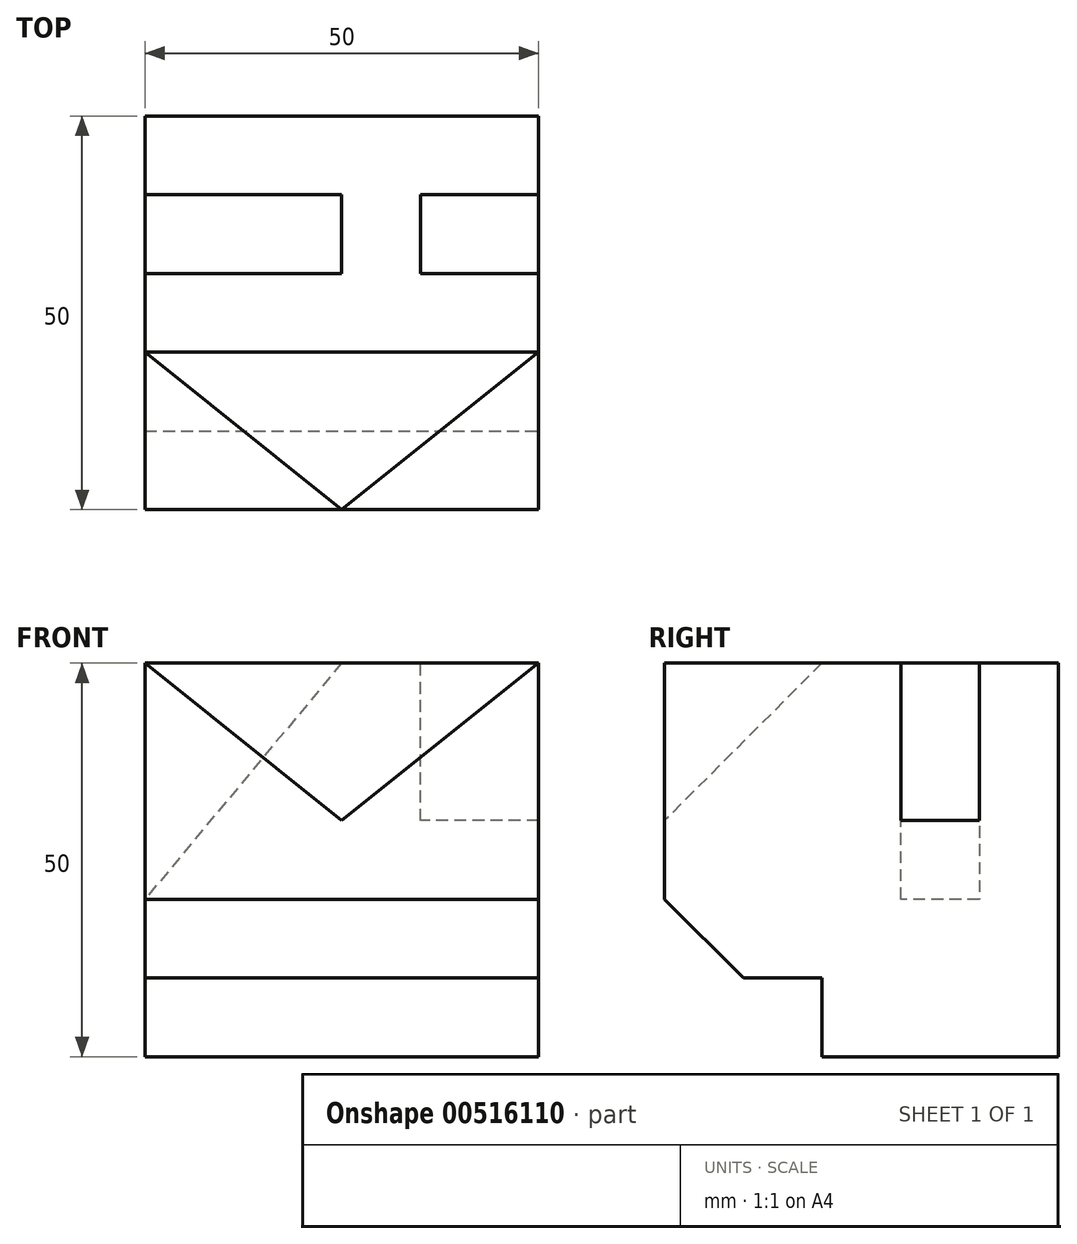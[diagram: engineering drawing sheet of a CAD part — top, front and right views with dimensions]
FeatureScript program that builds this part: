
annotation { "Feature Type Name" : "Feature", "Feature Type Description" : "" }
export const myFeature = defineFeature(function(context is Context, id is Id, definition is map)
    precondition{}
    {
        {
            var Q0;
            Q0=qCreatedBy(makeId("Top.planeOp"),FACE);
            var sketch = newSketch(context, id + "F0", { "sketchPlane" : qUnion([Q0])});
            skLineSegment(sketch, "E0.bottom", {"start": v(0, 0) * mm, "end": v(50, 0) * mm});
            skLineSegment(sketch, "E0.top", {"start": v(0, 50) * mm, "end": v(50, 50) * mm});
            skLineSegment(sketch, "E0.left", {"start": v(0, 0) * mm, "end": v(0, 50) * mm});
            skLineSegment(sketch, "E0.right", {"start": v(50, 0) * mm, "end": v(50, 50) * mm});
            skSolve(sketch);
        }
        {
            var Q0;
            Q0=makeQuery(id+"F0.imprint","IMPRINT",FACE,{"disambiguationData":[TD([[makeQuery(id+"F0.imprint","IMPRINT",EDGE,{"derivedFrom":sQuery(id+"F0.wireOp",EDGE,"E0.bottom")}),1.0]])]});
            extrude(context, id + "F1", {"entities" : qUnion([Q0]), "depth" : 50 * mm, "offsetDistance" : 25 * mm});
        }
        {
            var Q0;
            Q0=makeQuery(id+"F1.opExtrude","SWEPT_FACE",FACE,{"disambiguationData":[OSD([sQuery(id+"F0.wireOp",EDGE,"E0.right")])]});
            var sketch = newSketch(context, id + "F2", { "sketchPlane" : qUnion([Q0])});
            skLineSegment(sketch, "E1.bottom", {"start": v(0, 0) * mm, "end": v(20, 0) * mm});
            skLineSegment(sketch, "E1.top", {"start": v(0, 10) * mm, "end": v(20, 10) * mm});
            skLineSegment(sketch, "E1.left", {"start": v(0, 0) * mm, "end": v(0, 10) * mm});
            skLineSegment(sketch, "E1.right", {"start": v(20, 0) * mm, "end": v(20, 10) * mm});
            skSolve(sketch);
        }
        {
            var Q0;
            Q0=makeQuery(id+"F2.imprint","IMPRINT",FACE,{"disambiguationData":[TD([[makeQuery(id+"F2.imprint","IMPRINT",EDGE,{"derivedFrom":sQuery(id+"F2.wireOp",EDGE,"E1.bottom")}),1.0]])]});
            extrude(context, id + "F3", {"entities" : qUnion([Q0]), "operationType" : NewBodyOperationType.REMOVE, "endBound" : BoundingType.THROUGH_ALL, "oppositeDirection" : true, "depth" : 25 * mm, "offsetDistance" : 25 * mm});
        }
        {
            var Q0;
            Q0=makeQuery(id+"F1.opExtrude","SWEPT_FACE",FACE,{"disambiguationData":[OSD([sQuery(id+"F0.wireOp",EDGE,"E0.right")])]});
            var sketch = newSketch(context, id + "F4", { "sketchPlane" : qUnion([Q0])});
            skLineSegment(sketch, "E2", {"start": v(0, 10) * mm, "end": v(10, 10) * mm});
            skLineSegment(sketch, "E3", {"start": v(10, 10) * mm, "end": v(0, 20) * mm});
            skLineSegment(sketch, "E4", {"start": v(0, 20) * mm, "end": v(0, 10) * mm});
            skSolve(sketch);
        }
        {
            var Q0;
            Q0=makeQuery(id+"F4.imprint","IMPRINT",FACE,{"disambiguationData":[TD([[makeQuery(id+"F4.imprint","IMPRINT",EDGE,{"derivedFrom":sQuery(id+"F4.wireOp",EDGE,"E2")}),1.0]])]});
            extrude(context, id + "F5", {"entities" : qUnion([Q0]), "operationType" : NewBodyOperationType.REMOVE, "endBound" : BoundingType.THROUGH_ALL, "oppositeDirection" : true, "depth" : 25 * mm, "offsetDistance" : 25 * mm});
        }
        {
            var Q0;
            Q0=makeQuery(id+"F1.opExtrude","CAP_FACE",FACE,{"disambiguationData":[OSD([sQuery(id+"F0.wireOp",EDGE,"E0.bottom"),sQuery(id+"F0.wireOp",EDGE,"E0.top"),sQuery(id+"F0.wireOp",EDGE,"E0.left"),sQuery(id+"F0.wireOp",EDGE,"E0.right")])],"isStart":false});
            var sketch = newSketch(context, id + "F6", { "sketchPlane" : qUnion([Q0])});
            skLineSegment(sketch, "E5.bottom", {"start": v(0, 40) * mm, "end": v(25, 40) * mm});
            skLineSegment(sketch, "E5.top", {"start": v(0, 30) * mm, "end": v(25, 30) * mm});
            skLineSegment(sketch, "E5.left", {"start": v(0, 40) * mm, "end": v(0, 30) * mm});
            skLineSegment(sketch, "E5.right", {"start": v(25, 40) * mm, "end": v(25, 30) * mm});
            skSolve(sketch);
        }
        {
            var Q0;
            Q0=makeQuery(id+"F1.opExtrude","SWEPT_FACE",FACE,{"disambiguationData":[OSD([sQuery(id+"F0.wireOp",EDGE,"E0.bottom")])]});
            var sketch = newSketch(context, id + "F7", { "sketchPlane" : qUnion([Q0])});
            skLineSegment(sketch, "E6", {"start": v(25, 50) * mm, "end": v(0, 20) * mm});
            skSolve(sketch);
        }
        {
            var Q0;
            Q0=makeQuery(id+"F6.imprint","IMPRINT",FACE,{"disambiguationData":[TD([[makeQuery(id+"F6.imprint","IMPRINT",EDGE,{"derivedFrom":sQuery(id+"F6.wireOp",EDGE,"E5.bottom")}),-1.0]])]});
            var Q1;
            Q1=sQuery(id+"F7.wireOp",EDGE,"E6");
            sweep(context, id + "F8", {"operationType" : NewBodyOperationType.REMOVE, "profiles" : qUnion([Q0]), "path" : qUnion([Q1])});
        }
        {
            var Q0;
            Q0=makeQuery(id+"F1.opExtrude","CAP_FACE",FACE,{"disambiguationData":[OSD([sQuery(id+"F0.wireOp",EDGE,"E0.bottom"),sQuery(id+"F0.wireOp",EDGE,"E0.top"),sQuery(id+"F0.wireOp",EDGE,"E0.left"),sQuery(id+"F0.wireOp",EDGE,"E0.right")])],"isStart":false});
            var sketch = newSketch(context, id + "F9", { "sketchPlane" : qUnion([Q0])});
            skLineSegment(sketch, "E7.bottom", {"start": v(50, 40) * mm, "end": v(35, 40) * mm});
            skLineSegment(sketch, "E7.top", {"start": v(50, 30) * mm, "end": v(35, 30) * mm});
            skLineSegment(sketch, "E7.left", {"start": v(50, 40) * mm, "end": v(50, 30) * mm});
            skLineSegment(sketch, "E7.right", {"start": v(35, 40) * mm, "end": v(35, 30) * mm});
            skSolve(sketch);
        }
        {
            var Q0;
            Q0=makeQuery(id+"F9.imprint","IMPRINT",FACE,{"disambiguationData":[TD([[makeQuery(id+"F9.imprint","IMPRINT",EDGE,{"derivedFrom":sQuery(id+"F9.wireOp",EDGE,"E7.bottom")}),1.0]])]});
            extrude(context, id + "F10", {"entities" : qUnion([Q0]), "operationType" : NewBodyOperationType.REMOVE, "oppositeDirection" : true, "depth" : 20 * mm, "offsetDistance" : 25 * mm});
        }
        {
            var Q0;
            Q0=makeQuery(id+"F1.opExtrude","SWEPT_FACE",FACE,{"disambiguationData":[OSD([sQuery(id+"F0.wireOp",EDGE,"E0.bottom")])]});
            var sketch = newSketch(context, id + "F11", { "sketchPlane" : qUnion([Q0])});
            skLineSegment(sketch, "E8", {"start": v(0, 50) * mm, "end": v(25, 30) * mm});
            skLineSegment(sketch, "E9", {"start": v(25, 30) * mm, "end": v(50, 50) * mm});
            skSolve(sketch);
        }
        {
            var Q0;
            Q0=makeQuery(id+"F1.opExtrude","CAP_FACE",FACE,{"disambiguationData":[OSD([sQuery(id+"F0.wireOp",EDGE,"E0.bottom"),sQuery(id+"F0.wireOp",EDGE,"E0.top"),sQuery(id+"F0.wireOp",EDGE,"E0.left"),sQuery(id+"F0.wireOp",EDGE,"E0.right")])],"isStart":false});
            var sketch = newSketch(context, id + "F12", { "sketchPlane" : qUnion([Q0])});
            skLineSegment(sketch, "E10", {"start": v(0, 20) * mm, "end": v(50, 20) * mm});
            skSolve(sketch);
        }
        {
            var Q0;
            Q0=sQuery(id+"F12.wireOp",VERTEX,"E10.start");
            var Q1;
            Q1=sQuery(id+"F12.wireOp",VERTEX,"E10.end");
            var Q2;
            Q2=sQuery(id+"F11.wireOp",VERTEX,"E9.start");
            cPlane(context, id + "F13", {"entities" : qUnion([Q0, Q1, Q2]), "cplaneType" : CPlaneType.THREE_POINT, "offset" : 25 * mm, "width" : 150 * mm, "height" : 150 * mm});
        }
        {
            var Q0;
            Q0=makeQuery(id+"F11.imprint","IMPRINT",FACE,{"disambiguationData":[TD([[makeQuery(id+"F11.imprint","IMPRINT",EDGE,{"derivedFrom":sQuery(id+"F11.wireOp",EDGE,"E8")}),1.0]])]});
            extrude(context, id + "F14", {"entities" : qUnion([Q0]), "operationType" : NewBodyOperationType.REMOVE, "oppositeDirection" : true, "depth" : 20 * mm, "offsetDistance" : 25 * mm});
        }
        {
            var Q0;
            Q0=makeQuery(id+"F14.boolean.opBoolean","COPY",FACE,{"derivedFrom":makeQuery(id+"F14.opExtrude","CAP_FACE",FACE,{"disambiguationData":[OSD([sQuery(id+"F0.wireOp",EDGE,"E0.bottom"),sQuery(id+"F11.wireOp",EDGE,"E8"),sQuery(id+"F11.wireOp",EDGE,"E9")])],"isStart":false})});
            var Q1;
            Q1=qCreatedBy(id+"F13.planeOp",FACE);
            extrude(context, id + "F15", {"entities" : qUnion([Q0]), "operationType" : NewBodyOperationType.ADD, "endBound" : BoundingType.UP_TO_SURFACE, "depth" : 25 * mm, "endBoundEntityFace" : qUnion([Q1]), "offsetDistance" : 25 * mm});
        }
    });
